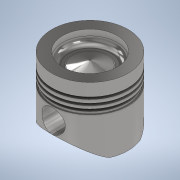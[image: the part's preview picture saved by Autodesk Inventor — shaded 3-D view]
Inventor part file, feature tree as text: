
AUTODESK INVENTOR PART (.ipt)
format: ipt  version: 2021 (Build 250183000, 183)  size: 298,496 bytes
history: native  units: mm
features: sketch x4, extrude x3, other x2, revolve x2, mirror x1
ambient origin geometry x8: Origin, YZ Plane, XZ Plane, XY Plane, X Axis, Y Axis, Z Axis, Center Point
bodies: Body1 (feature_tree)
feature tree (12):
  other  "Твердое тело1"
  revolve  "Вращение1"
  revolve  "Вращение2"
  extrude  "Выдавливание1"  Depth=80.0mm
  other  "РабПлоскость1"
  extrude  "Выдавливание2"  Depth=45.55mm
  mirror  "Зеркальное отражение1"
  extrude  "Выдавливание3"  Depth=13.0mm
  sketch  "Эскиз2"
  sketch  "Эскиз3"
  sketch  "Эскиз4"
  sketch  "Эскиз5"
